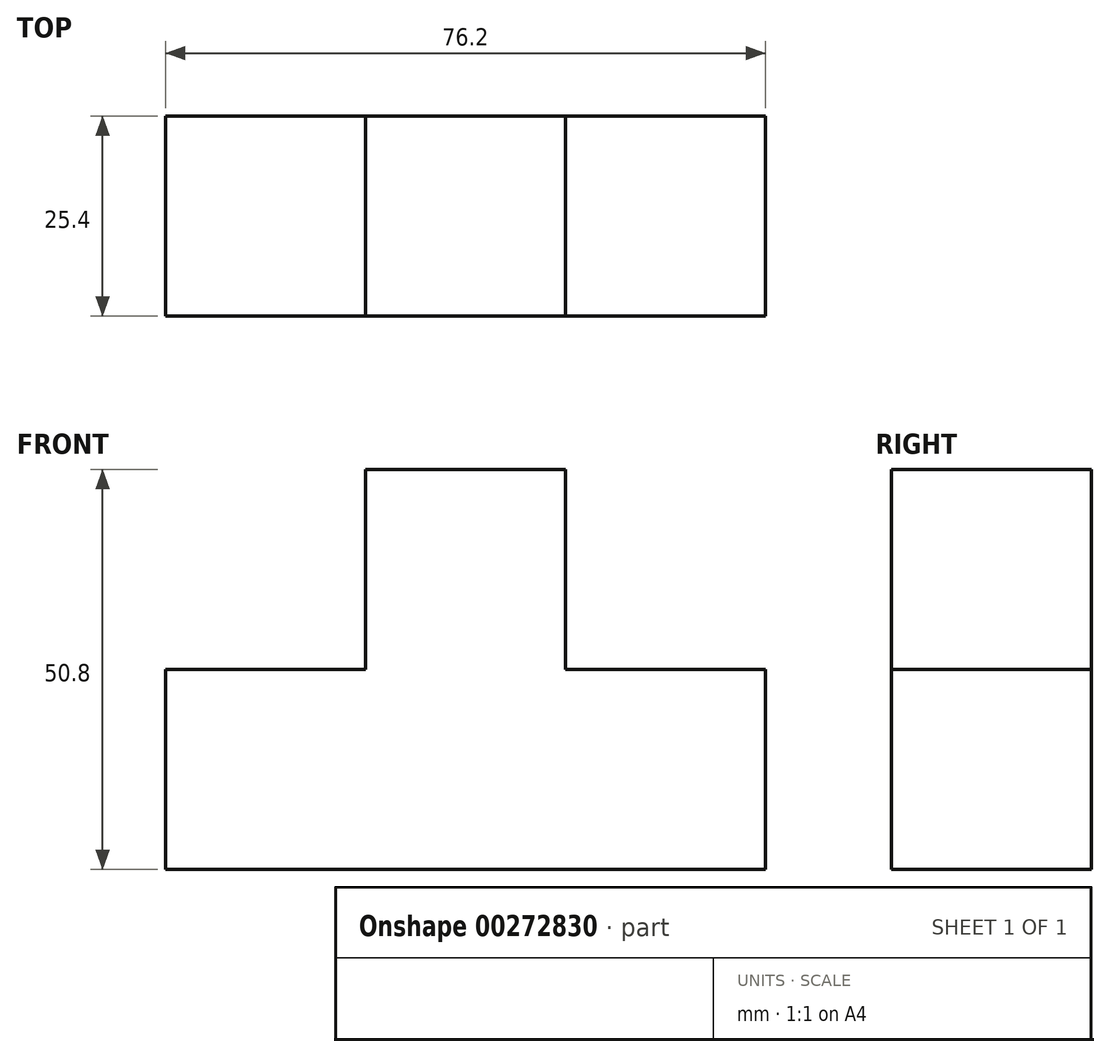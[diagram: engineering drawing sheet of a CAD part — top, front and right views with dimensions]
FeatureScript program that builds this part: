
annotation { "Feature Type Name" : "Feature", "Feature Type Description" : "" }
export const myFeature = defineFeature(function(context is Context, id is Id, definition is map)
    precondition{}
    {
        {
            var Q0;
            Q0=qCreatedBy(makeId("Front.planeOp"),FACE);
            var sketch = newSketch(context, id + "F0", { "sketchPlane" : qUnion([Q0])});
            skLineSegment(sketch, "E0", {"start": v(0, 0) * mm, "end": v(-76.2, 0) * mm});
            skLineSegment(sketch, "E1", {"start": v(-76.2, 0) * mm, "end": v(-76.2, 25.4) * mm});
            skLineSegment(sketch, "E2", {"start": v(-76.2, 25.4) * mm, "end": v(-50.8, 25.4) * mm});
            skLineSegment(sketch, "E3", {"start": v(-50.8, 25.4) * mm, "end": v(-50.8, 50.8) * mm});
            skLineSegment(sketch, "E4", {"start": v(-50.8, 50.8) * mm, "end": v(-25.4, 50.8) * mm});
            skLineSegment(sketch, "E5", {"start": v(-25.4, 50.8) * mm, "end": v(-25.4, 25.4) * mm});
            skLineSegment(sketch, "E6", {"start": v(-25.4, 25.4) * mm, "end": v(0, 25.4) * mm});
            skLineSegment(sketch, "E7", {"start": v(0, 25.4) * mm, "end": v(0, 0) * mm});
            skSolve(sketch);
        }
        {
            var Q0;
            Q0=makeQuery(id+"F0.imprint","IMPRINT",FACE,{"disambiguationData":[TD([[makeQuery(id+"F0.imprint","IMPRINT",EDGE,{"derivedFrom":sQuery(id+"F0.wireOp",EDGE,"E0")}),-1.0]])]});
            extrude(context, id + "F1", {"entities" : qUnion([Q0]), "depth" : 25.4 * mm});
        }
    });
